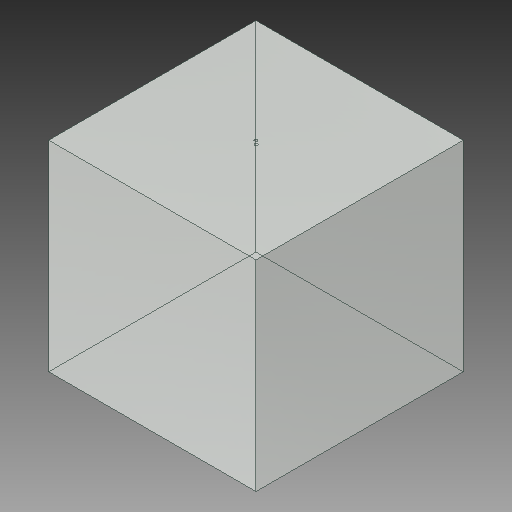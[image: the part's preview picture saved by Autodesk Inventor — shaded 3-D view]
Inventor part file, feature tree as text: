
AUTODESK INVENTOR PART (.ipt)
format: ipt  version: 2019 (Build 230136000, 136)  size: 99,328 bytes
history: native  units: mm
features: extrude x2, sketch x2
ambient origin geometry x8: Origin, YZ Plane, XZ Plane, XY Plane, X Axis, Y Axis, Z Axis, Center Point
bodies: Solid1 (feature_tree)
feature tree (4):
  extrude  "Extrusion1"  Depth=276.0mm
  extrude  "Extrusion2"  Depth=5.0mm
  sketch  "Sketch1"  dims[d0=276.0mm d1=276.0mm]
  sketch  "Sketch2"  dims[d2=267.0mm d3=0.0mm d4=4.0mm d5=138.0mm d6=5.0mm d7=0.0mm]
